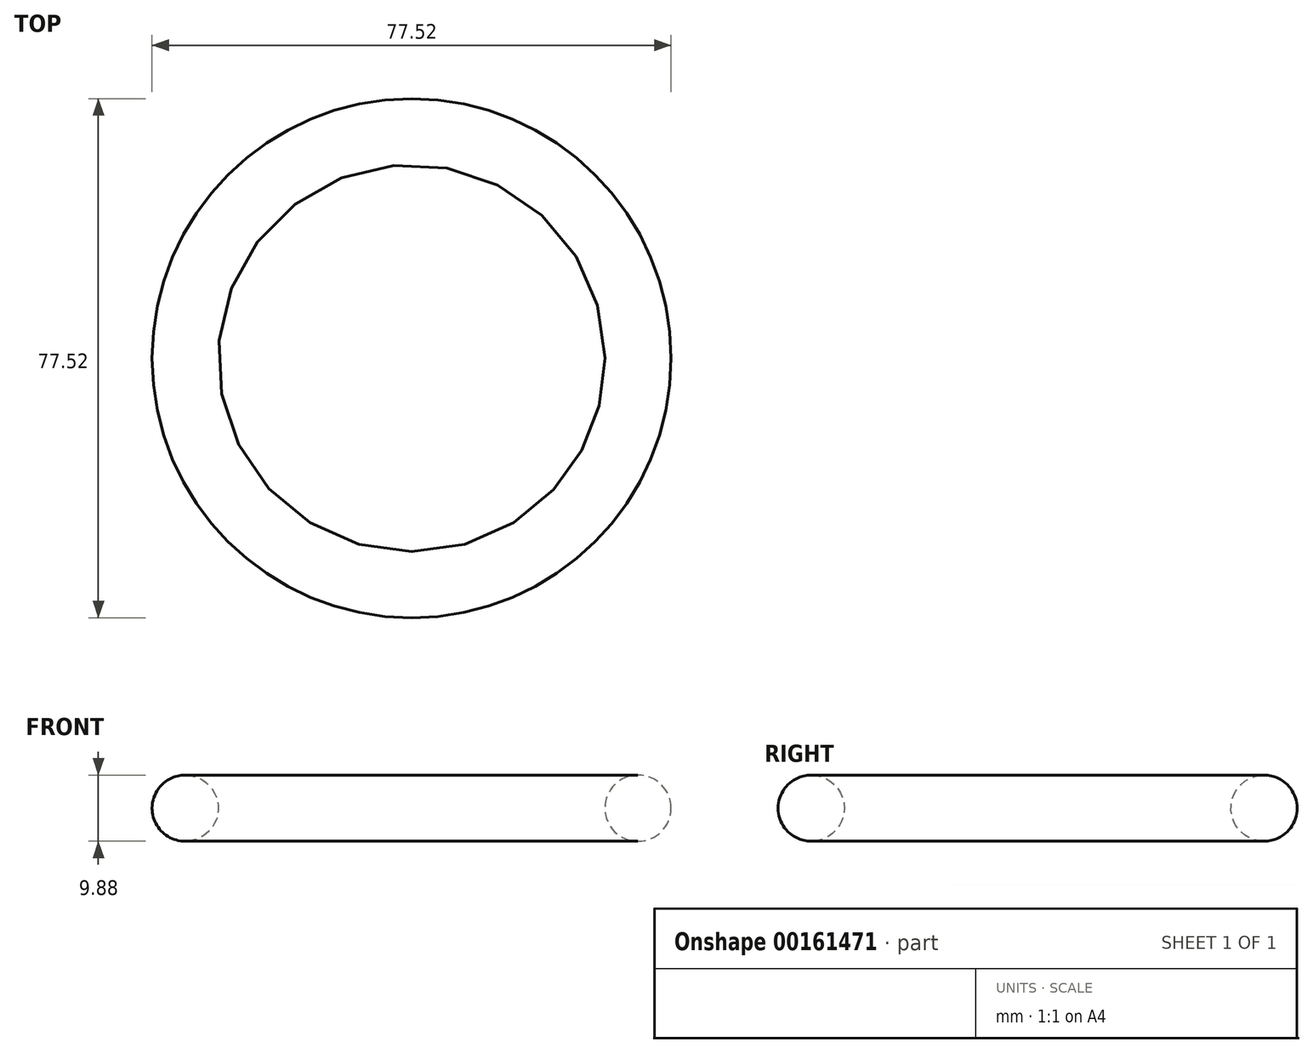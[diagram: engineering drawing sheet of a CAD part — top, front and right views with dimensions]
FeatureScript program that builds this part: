
annotation { "Feature Type Name" : "Feature", "Feature Type Description" : "" }
export const myFeature = defineFeature(function(context is Context, id is Id, definition is map)
    precondition{}
    {
        {
            var Q0;
            Q0=qCreatedBy(makeId("Front.planeOp"),FACE);
            var sketch = newSketch(context, id + "F0", { "sketchPlane" : qUnion([Q0])});
            skCircle(sketch, "E0", {"center": v(33.82, 0) * mm, "radius": 4.94 * mm});
            skLineSegment(sketch, "E1", {"start": v(0, 0) * mm, "end": v(0, 42.5) * mm, "construction": true});
            skSolve(sketch);
        }
        {
            var Q0;
            Q0=sQuery(id+"F0.wireOp",EDGE,"E0");
            var Q1;
            Q1=sQuery(id+"F0.wireOp",EDGE,"E1");
            revolve(context, id + "F1", {"bodyType" : ToolBodyType.SURFACE, "surfaceEntities" : qUnion([Q0]), "axis" : qUnion([Q1]), "revolveType" : RevolveType.FULL});
        }
    });
